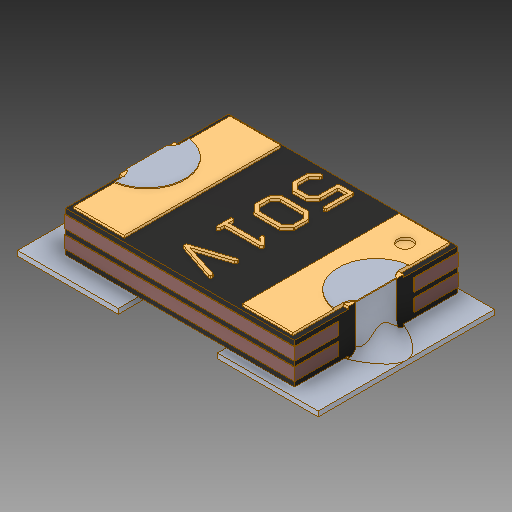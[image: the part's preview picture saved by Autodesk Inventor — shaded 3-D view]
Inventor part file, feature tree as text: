
AUTODESK INVENTOR PART (.ipt)
format: ipt  version: 2018.2 (Build 222227000, 227)  size: 402,944 bytes
history: native  units: mm
features: mirror x1
ambient origin geometry x8: Origin, YZ Plane, XZ Plane, XY Plane, X Axis, Y Axis, Z Axis, Center Point
bodies: Solido1 (feature_tree)
feature tree (1):
  mirror  "Mirror5"
